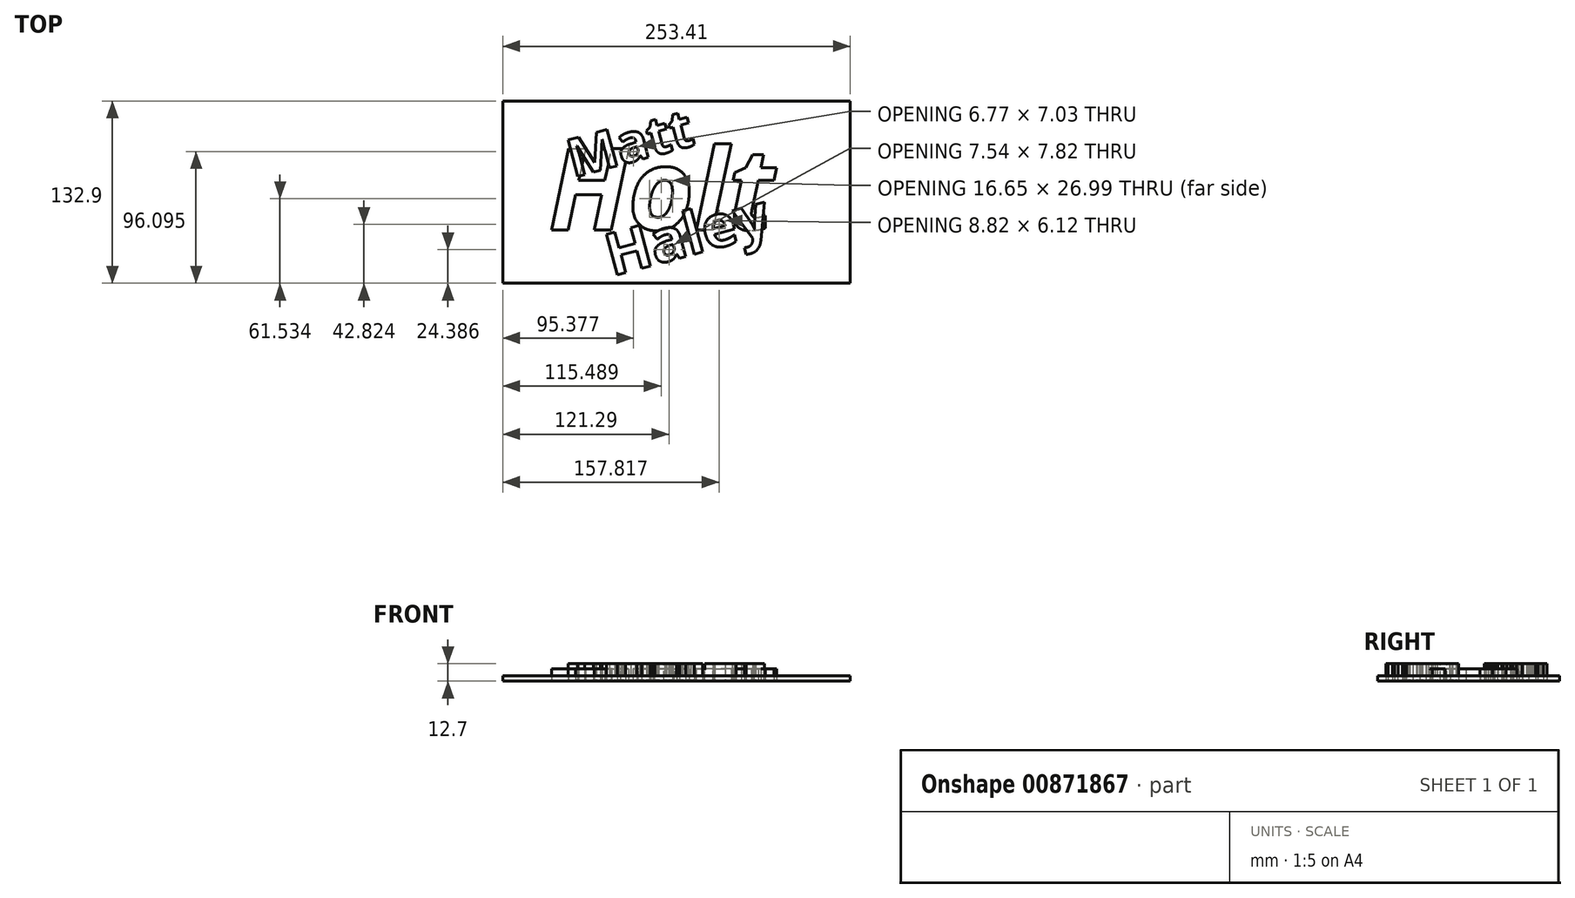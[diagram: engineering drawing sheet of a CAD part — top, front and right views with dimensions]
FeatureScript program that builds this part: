
annotation { "Feature Type Name" : "Feature", "Feature Type Description" : "" }
export const myFeature = defineFeature(function(context is Context, id is Id, definition is map)
    precondition{}
    {
        {
            var Q0;
            Q0=qCreatedBy(makeId("Top.planeOp"),FACE);
            var sketch = newSketch(context, id + "F0", { "sketchPlane" : qUnion([Q0])});
            skText(sketch, "E0", { "text": "Holt", "fontName": "OpenSans-BoldItalic.ttf"});
            const initialGuessF0  = {"E0": [-0.08711, -0.03158, 1, 0, 0.05957]};
            skSetInitialGuess(sketch, initialGuessF0);
            skSolve(sketch);
        }
        {
            var Q0;
            Q0=qCreatedBy(makeId("Top.planeOp"),FACE);
            var sketch = newSketch(context, id + "F1", { "sketchPlane" : qUnion([Q0])});
            skText(sketch, "E1", { "text": "Matt", "fontName": "OpenSans-Bold.ttf"});
            const initialGuessF1  = {"E1": [-0.06904, 0.00648, 0.96593, 0.25882, 0.02772]};
            skSetInitialGuess(sketch, initialGuessF1);
            skSolve(sketch);
        }
        {
            var Q0;
            Q0=qCreatedBy(makeId("Top.planeOp"),FACE);
            var sketch = newSketch(context, id + "F2", { "sketchPlane" : qUnion([Q0])});
            skText(sketch, "E2", { "text": "Haley", "fontName": "OpenSans-Bold.ttf"});
            const initialGuessF2  = {"E2": [-0.04075, -0.06542, 0.96593, 0.25882, 0.03086]};
            skSetInitialGuess(sketch, initialGuessF2);
            skSolve(sketch);
        }
        {
            var Q0;
            Q0=makeQuery(id+"F0.imprint","IMPRINT",FACE,{"disambiguationData":[TD([[makeQuery(id+"F0.imprint","IMPRINT",EDGE,{"derivedFrom":sQuery(id+"F0.wireOp",EDGE,"E0.sketch_text.stroke-0")}),-1.0]])]});
            var Q1;
            Q1 = qSketchRegion(id + "F0", true);
            extrude(context, id + "F3", {"entities" : qUnion([Q0, Q1]), "depth" : 8.9 * mm, "offsetDistance" : 25.4 * mm});
        }
        {
            var Q0;
            Q0 = qSketchRegion(id + "F1", true);
            extrude(context, id + "F4", {"entities" : qUnion([Q0]), "depth" : 12.7 * mm, "offsetDistance" : 25.4 * mm});
        }
        {
            var Q0;
            Q0 = qSketchRegion(id + "F2", true);
            extrude(context, id + "F5", {"entities" : qUnion([Q0]), "depth" : 12.7 * mm, "offsetDistance" : 25.4 * mm});
        }
        {
            var Q0;
            Q0=qCreatedBy(makeId("Top.planeOp"),FACE);
            var sketch = newSketch(context, id + "F6", { "sketchPlane" : qUnion([Q0])});
            skLineSegment(sketch, "E3.bottom", {"start": v(-120.47, 62.37) * mm, "end": v(132.94, 62.37) * mm});
            skLineSegment(sketch, "E3.top", {"start": v(-120.47, -70.53) * mm, "end": v(132.94, -70.53) * mm});
            skLineSegment(sketch, "E3.left", {"start": v(-120.47, 62.37) * mm, "end": v(-120.47, -70.53) * mm});
            skLineSegment(sketch, "E3.right", {"start": v(132.94, 62.37) * mm, "end": v(132.94, -70.53) * mm});
            skSolve(sketch);
        }
        {
            var Q0;
            Q0 = qSketchRegion(id + "F6", true);
            extrude(context, id + "F7", {"entities" : qUnion([Q0]), "depth" : 3.8 * mm, "offsetDistance" : 25.4 * mm});
        }
    });
